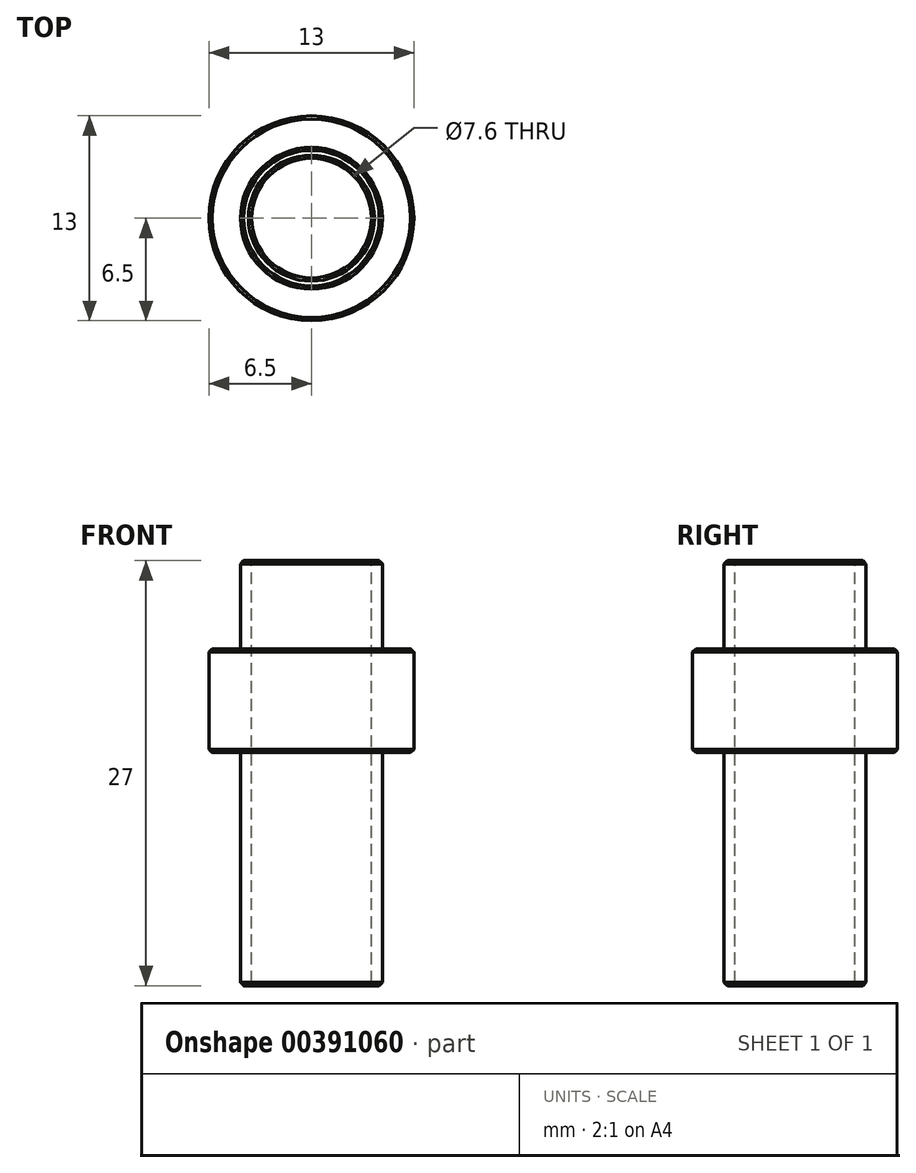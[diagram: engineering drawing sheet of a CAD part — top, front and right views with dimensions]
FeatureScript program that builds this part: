
annotation { "Feature Type Name" : "Feature", "Feature Type Description" : "" }
export const myFeature = defineFeature(function(context is Context, id is Id, definition is map)
    precondition{}
    {
        {
            var Q0;
            Q0=qCreatedBy(makeId("Front.planeOp"),FACE);
            var sketch = newSketch(context, id + "F0", { "sketchPlane" : qUnion([Q0])});
            skLineSegment(sketch, "E0", {"start": v(3.8, 0) * mm, "end": v(3.8, 27) * mm});
            skLineSegment(sketch, "E1", {"start": v(3.8, 27) * mm, "end": v(4.5, 27) * mm});
            skLineSegment(sketch, "E2", {"start": v(4.5, 27) * mm, "end": v(4.5, 21.4) * mm});
            skLineSegment(sketch, "E3", {"start": v(4.5, 21.4) * mm, "end": v(6.5, 21.4) * mm});
            skLineSegment(sketch, "E4", {"start": v(6.5, 21.4) * mm, "end": v(6.5, 14.8) * mm});
            skLineSegment(sketch, "E5", {"start": v(6.5, 14.8) * mm, "end": v(4.5, 14.8) * mm});
            skLineSegment(sketch, "E6", {"start": v(4.5, 14.8) * mm, "end": v(4.5, 0) * mm});
            skLineSegment(sketch, "E7", {"start": v(4.5, 0) * mm, "end": v(3.8, 0) * mm});
            skLineSegment(sketch, "E8", {"start": v(0, 100) * mm, "end": v(0, 0) * mm, "construction": true});
            skSolve(sketch);
        }
        {
            var Q0;
            Q0=makeQuery(id+"F0.imprint","IMPRINT",FACE,{"disambiguationData":[TD([[makeQuery(id+"F0.imprint","IMPRINT",EDGE,{"derivedFrom":sQuery(id+"F0.wireOp",EDGE,"E0")}),-1.0]])]});
            var Q1;
            Q1=sQuery(id+"F0.wireOp",EDGE,"E8");
            var Q2;
            Q2=sQuery(id+"F0.wireOp",EDGE,"E8");
            revolve(context, id + "F1", {"entities" : qUnion([Q0]), "surfaceEntities" : qUnion([Q1]), "axis" : qUnion([Q2]), "revolveType" : RevolveType.FULL});
        }
        {
            var Q0;
            Q0=makeQuery(id+"F1.opRevolve","SWEPT_EDGE",EDGE,{"disambiguationData":[OSD([sQuery(id+"F0.wireOp",EDGE,"E6"),sQuery(id+"F0.wireOp",EDGE,"E7")])]});
            var Q1;
            Q1=makeQuery(id+"F1.opRevolve","SWEPT_EDGE",EDGE,{"disambiguationData":[OSD([sQuery(id+"F0.wireOp",EDGE,"E4"),sQuery(id+"F0.wireOp",EDGE,"E5")])]});
            var Q2;
            Q2=makeQuery(id+"F1.opRevolve","SWEPT_EDGE",EDGE,{"disambiguationData":[OSD([sQuery(id+"F0.wireOp",EDGE,"E3"),sQuery(id+"F0.wireOp",EDGE,"E4")])]});
            var Q3;
            Q3=makeQuery(id+"F1.opRevolve","SWEPT_EDGE",EDGE,{"disambiguationData":[OSD([sQuery(id+"F0.wireOp",EDGE,"E1"),sQuery(id+"F0.wireOp",EDGE,"E2")])]});
            var Q4;
            Q4=makeQuery(id+"F1.opRevolve","SWEPT_EDGE",EDGE,{"disambiguationData":[OSD([sQuery(id+"F0.wireOp",EDGE,"E0"),sQuery(id+"F0.wireOp",EDGE,"E1")])]});
            var Q5;
            Q5=makeQuery(id+"F1.opRevolve","SWEPT_EDGE",EDGE,{"disambiguationData":[OSD([sQuery(id+"F0.wireOp",EDGE,"E0"),sQuery(id+"F0.wireOp",EDGE,"E7")])]});
            chamfer(context, id + "F2", {"entities" : qUnion([Q0, Q1, Q2, Q3, Q4, Q5]), "width" : .2 * mm, "tangentPropagation" : true});
        }
    });
